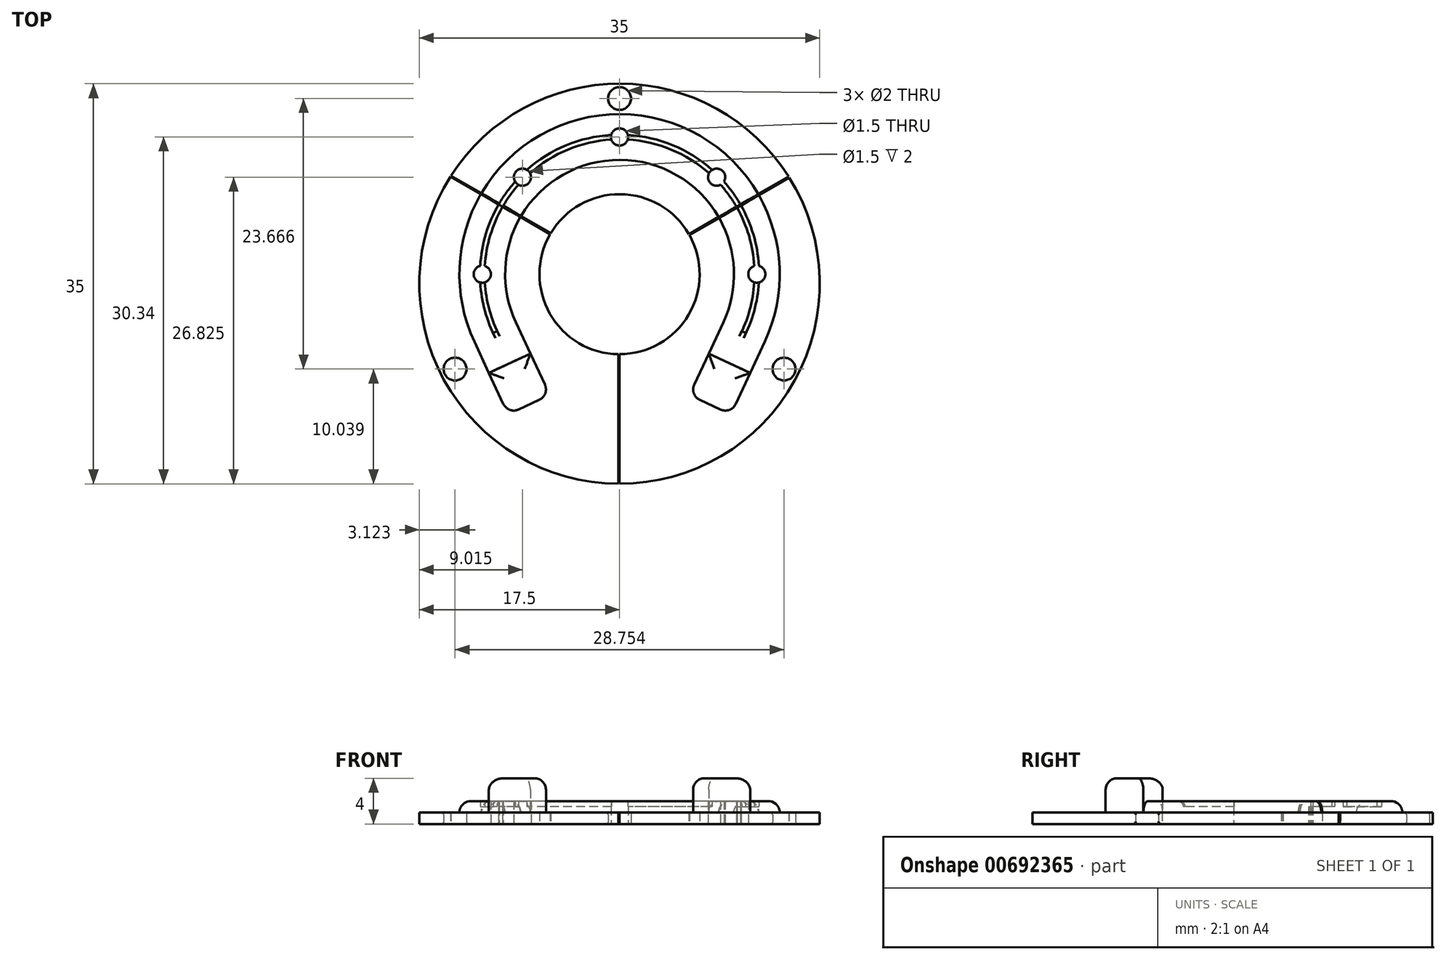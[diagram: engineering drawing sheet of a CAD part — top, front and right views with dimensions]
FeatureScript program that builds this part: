
annotation { "Feature Type Name" : "Feature", "Feature Type Description" : "" }
export const myFeature = defineFeature(function(context is Context, id is Id, definition is map)
    precondition{}
    {
        {
            var Q0;
            Q0=qCreatedBy(makeId("Top.planeOp"),FACE);
            var sketch = newSketch(context, id + "F0", { "sketchPlane" : qUnion([Q0])});
            skFitSpline(sketch, "E0", {"points": [v(-1.42, -15.36) * mm, v(0, -15.45) * mm, v(1.43, -15.36) * mm, v(3.29, -15.03) * mm, v(5.07, -14.39) * mm, v(6.72, -13.46) * mm, v(8.27, -12.35) * mm, v(9.96, -10.69) * mm, v(11.3, -8.73) * mm, v(12.17, -7) * mm, v(12.88, -5.22) * mm, v(13.35, -3.36) * mm, v(13.59, -1.45) * mm, v(13.65, 0) * mm, v(13.59, 1.45) * mm, v(13.35, 3.36) * mm, v(12.88, 5.23) * mm, v(12.17, 7) * mm, v(11.3, 8.73) * mm, v(9.96, 10.69) * mm, v(8.27, 12.35) * mm, v(6.72, 13.46) * mm, v(5.07, 14.4) * mm, v(3.29, 15.04) * mm, v(1.43, 15.37) * mm, v(0, 15.45) * mm, v(-1.42, 15.37) * mm, v(-3.28, 15.04) * mm, v(-5.07, 14.4) * mm, v(-6.72, 13.46) * mm, v(-8.26, 12.35) * mm, v(-9.96, 10.69) * mm, v(-11.3, 8.73) * mm, v(-12.17, 7) * mm, v(-12.87, 5.23) * mm, v(-13.35, 3.36) * mm, v(-13.58, 1.45) * mm, v(-13.64, 0) * mm, v(-13.58, -1.45) * mm, v(-13.35, -3.36) * mm, v(-12.87, -5.22) * mm, v(-12.17, -7) * mm, v(-11.3, -8.73) * mm, v(-9.96, -10.69) * mm, v(-8.26, -12.35) * mm, v(-6.72, -13.46) * mm, v(-5.07, -14.39) * mm, v(-3.28, -15.03) * mm, v(-1.42, -15.36) * mm, v(0, -15.45) * mm, v(1.43, -15.36) * mm]});
            skLineSegment(sketch, "E1", {"start": v(0, 0) * mm, "end": v(-9.06, -4.23) * mm});
            skLineSegment(sketch, "E2", {"start": v(0, 0) * mm, "end": v(9.06, -4.23) * mm});
            skLineSegment(sketch, "E3", {"start": v(-9.06, -4.23) * mm, "end": v(-9.06, -4.23) * mm});
            skLineSegment(sketch, "E4", {"start": v(9.06, -4.23) * mm, "end": v(12.69, -5.92) * mm});
            skLineSegment(sketch, "E5", {"start": v(-9.06, -4.23) * mm, "end": v(-12.69, -5.92) * mm});
            skArc(sketch, "E6", {"start": v(9.06, -4.23) * mm, "mid": v(0, 10) * mm, "end": v(-9.06, -4.23) * mm});
            skArc(sketch, "E7", {"start": v(12.69, -5.92) * mm, "mid": v(0, 14) * mm, "end": v(-12.69, -5.92) * mm});
            skLineSegment(sketch, "E8", {"start": v(-9.06, -4.23) * mm, "end": v(-6.1, -10.57) * mm});
            skLineSegment(sketch, "E9", {"start": v(-6.1, -10.57) * mm, "end": v(-9.73, -12.26) * mm});
            skLineSegment(sketch, "E10", {"start": v(-9.73, -12.26) * mm, "end": v(-12.69, -5.92) * mm});
            skLineSegment(sketch, "E11", {"start": v(9.06, -4.23) * mm, "end": v(6.1, -10.57) * mm});
            skLineSegment(sketch, "E12", {"start": v(6.1, -10.57) * mm, "end": v(9.73, -12.26) * mm});
            skLineSegment(sketch, "E13", {"start": v(9.73, -12.26) * mm, "end": v(12.69, -5.92) * mm});
            skLineSegment(sketch, "E14", {"start": v(-7.8, -6.95) * mm, "end": v(-11.42, -8.64) * mm});
            skLineSegment(sketch, "E15", {"start": v(7.8, -6.95) * mm, "end": v(11.42, -8.64) * mm});
            skArc(sketch, "E16", {"start": v(-10.88, -5.07) * mm, "mid": v(0, 12) * mm, "end": v(10.88, -5.07) * mm});
            skLineSegment(sketch, "E17", {"start": v(0, 0) * mm, "end": v(8.49, 8.49) * mm});
            skLineSegment(sketch, "E18", {"start": v(0, 0) * mm, "end": v(-8.49, 8.49) * mm});
            skCircle(sketch, "E19", {"center": v(-12, 0) * mm, "radius": 0.75 * mm});
            skCircle(sketch, "E20", {"center": v(12, 0) * mm, "radius": 0.75 * mm});
            skCircle(sketch, "E21", {"center": v(8.49, 8.49) * mm, "radius": 0.75 * mm});
            skCircle(sketch, "E22", {"center": v(-8.49, 8.49) * mm, "radius": 0.75 * mm});
            skCircle(sketch, "E23", {"center": v(0, 12) * mm, "radius": 0.75 * mm});
            skArc(sketch, "E24.0", {"start": v(-10.7, -4.99) * mm, "mid": v(0, 11.8) * mm, "end": v(10.7, -4.99) * mm});
            skArc(sketch, "E25.0", {"start": v(-11.06, -5.16) * mm, "mid": v(0, 12.2) * mm, "end": v(11.06, -5.16) * mm});
            skPoint(sketch, "E26", {"position": v(0, -12.26) * mm});
            skPoint(sketch, "E27", {"position": v(0, -0.84) * mm});
            skCircle(sketch, "E28", {"center": v(0, -0.84) * mm, "radius": 17.5 * mm});
            skCircle(sketch, "E29", {"center": v(0, 0) * mm, "radius": 7 * mm});
            skPoint(sketch, "E30", {"position": v(0, 15.37) * mm});
            skLineSegment(sketch, "E31", {"start": v(0, 0) * mm, "end": v(-19.6, -11.31) * mm});
            skLineSegment(sketch, "E32", {"start": v(0, 0) * mm, "end": v(18.13, -10.47) * mm});
            skPoint(sketch, "E33", {"position": v(-14.38, -8.3) * mm});
            skPoint(sketch, "E34", {"position": v(14.38, -8.3) * mm});
            skCircle(sketch, "E35", {"center": v(0, 15.37) * mm, "radius": 1 * mm});
            skCircle(sketch, "E36", {"center": v(14.38, -8.3) * mm, "radius": 1 * mm});
            skCircle(sketch, "E37", {"center": v(-14.38, -8.3) * mm, "radius": 1 * mm});
            skLineSegment(sketch, "E38", {"start": v(0, 0) * mm, "end": v(0, -24.87) * mm});
            skLineSegment(sketch, "E39", {"start": v(0, 0) * mm, "end": v(19.52, 11.27) * mm});
            skLineSegment(sketch, "E40", {"start": v(0, 0) * mm, "end": v(-24.6, 14.2) * mm});
            skLineSegment(sketch, "E41.0", {"start": v(0.05, 0.09) * mm, "end": v(-24.54, 14.28) * mm});
            skLineSegment(sketch, "E42.0", {"start": v(0.05, -0.09) * mm, "end": v(19.57, 11.18) * mm});
            skLineSegment(sketch, "E43.0", {"start": v(-0.1, 0) * mm, "end": v(-0.1, -24.87) * mm});
            skSolve(sketch);
        }
        {
            var Q0;
            {var subQ5=sQuery(id+"F0.wireOp",EDGE,"E18");var subQ6=sQuery(id+"F0.wireOp",EDGE,"E6");var subQ7=makeQuery(id+"F0.imprint","INTERSECT",VERTEX,{"derivedFrom":[subQ6,subQ5]});Q0=makeQuery(id+"F0.imprint","IMPRINT",FACE,{"disambiguationData":[TD([[makeQuery(id+"F0.imprint","IMPRINT",EDGE,{"disambiguationData":[TD([[subQ7,-1.0]])],"derivedFrom":subQ6}),-1.0]])]});}
            var Q1;
            {var subQ0=sQuery(id+"F0.wireOp",EDGE,"E14");Q1=makeQuery(id+"F0.imprint","IMPRINT",FACE,{"disambiguationData":[TD([[makeQuery(id+"F0.imprint","IMPRINT",EDGE,{"derivedFrom":subQ0}),-1.0]])]});}
            var Q2;
            {var subQ0=sQuery(id+"F0.wireOp",EDGE,"E15");Q2=makeQuery(id+"F0.imprint","IMPRINT",FACE,{"disambiguationData":[TD([[makeQuery(id+"F0.imprint","IMPRINT",EDGE,{"derivedFrom":subQ0}),1.0]])]});}
            var Q3;
            {var subQ3=sQuery(id+"F0.wireOp",EDGE,"E39");var subQ7=sQuery(id+"F0.wireOp",EDGE,"E6");var subQ9=makeQuery(id+"F0.imprint","INTERSECT",VERTEX,{"derivedFrom":[subQ7,subQ3]});Q3=makeQuery(id+"F0.imprint","IMPRINT",FACE,{"disambiguationData":[TD([[makeQuery(id+"F0.imprint","IMPRINT",EDGE,{"disambiguationData":[TD([[subQ9,-1.0]])],"derivedFrom":subQ7}),-1.0]])]});}
            var Q4;
            {var subQ1=sQuery(id+"F0.wireOp",EDGE,"E17");var subQ9=sQuery(id+"F0.wireOp",EDGE,"E6");var subQ10=makeQuery(id+"F0.imprint","INTERSECT",VERTEX,{"derivedFrom":[subQ9,subQ1]});Q4=makeQuery(id+"F0.imprint","IMPRINT",FACE,{"disambiguationData":[TD([[makeQuery(id+"F0.imprint","IMPRINT",EDGE,{"disambiguationData":[TD([[subQ10,-1.0]])],"derivedFrom":subQ9}),-1.0]])]});}
            var Q5;
            {var subQ1=sQuery(id+"F0.wireOp",EDGE,"E5");var subQ4=makeQuery(id+"F0.imprint","INTERSECT",VERTEX,{"derivedFrom":[subQ1,sQuery(id+"F0.wireOp",EDGE,"E16")]});Q5=makeQuery(id+"F0.imprint","IMPRINT",FACE,{"disambiguationData":[TD([[makeQuery(id+"F0.imprint","IMPRINT",EDGE,{"disambiguationData":[TD([[subQ4,1.0]])],"derivedFrom":subQ1}),1.0]])]});}
            var Q6;
            {var subQ1=sQuery(id+"F0.wireOp",EDGE,"E4");var subQ4=makeQuery(id+"F0.imprint","INTERSECT",VERTEX,{"derivedFrom":[subQ1,sQuery(id+"F0.wireOp",EDGE,"E16")]});Q6=makeQuery(id+"F0.imprint","IMPRINT",FACE,{"disambiguationData":[TD([[makeQuery(id+"F0.imprint","IMPRINT",EDGE,{"disambiguationData":[TD([[subQ4,1.0]])],"derivedFrom":subQ1}),-1.0]])]});}
            var Q7;
            {var subQ6=sQuery(id+"F0.wireOp",EDGE,"E39");var subQ12=sQuery(id+"F0.wireOp",EDGE,"E7");var subQ13=makeQuery(id+"F0.imprint","INTERSECT",VERTEX,{"derivedFrom":[subQ12,subQ6]});Q7=makeQuery(id+"F0.imprint","IMPRINT",FACE,{"disambiguationData":[TD([[makeQuery(id+"F0.imprint","IMPRINT",EDGE,{"disambiguationData":[TD([[subQ13,-1.0]])],"derivedFrom":subQ12}),1.0]])]});}
            var Q8;
            {var subQ0=sQuery(id+"F0.wireOp",EDGE,"E24.0");var subQ1=sQuery(id+"F0.wireOp",EDGE,"E20");var subQ2=makeQuery(id+"F0.imprint","INTERSECT",VERTEX,{"disambiguationData":[OD(0.0)],"derivedFrom":[subQ1,subQ0]});Q8=makeQuery(id+"F0.imprint","IMPRINT",FACE,{"disambiguationData":[TD([[makeQuery(id+"F0.imprint","IMPRINT",EDGE,{"disambiguationData":[TD([[subQ2,-1.0]])],"derivedFrom":subQ1}),-1.0]])]});}
            var Q9;
            {var subQ0=sQuery(id+"F0.wireOp",EDGE,"E24.0");var subQ3=sQuery(id+"F0.wireOp",EDGE,"E19");var subQ5=makeQuery(id+"F0.imprint","INTERSECT",VERTEX,{"disambiguationData":[OD(0.0)],"derivedFrom":[subQ3,subQ0]});Q9=makeQuery(id+"F0.imprint","IMPRINT",FACE,{"disambiguationData":[TD([[makeQuery(id+"F0.imprint","IMPRINT",EDGE,{"disambiguationData":[TD([[subQ5,1.0]])],"derivedFrom":subQ3}),-1.0]])]});}
            var Q10;
            {var subQ0=sQuery(id+"F0.wireOp",EDGE,"E25.0");var subQ3=sQuery(id+"F0.wireOp",EDGE,"E19");var subQ5=makeQuery(id+"F0.imprint","INTERSECT",VERTEX,{"disambiguationData":[OD(0.0)],"derivedFrom":[subQ3,subQ0]});Q10=makeQuery(id+"F0.imprint","IMPRINT",FACE,{"disambiguationData":[TD([[makeQuery(id+"F0.imprint","IMPRINT",EDGE,{"disambiguationData":[TD([[subQ5,-1.0]])],"derivedFrom":subQ3}),-1.0]])]});}
            var Q11;
            {var subQ0=sQuery(id+"F0.wireOp",EDGE,"E25.0");var subQ1=sQuery(id+"F0.wireOp",EDGE,"E20");var subQ2=makeQuery(id+"F0.imprint","INTERSECT",VERTEX,{"disambiguationData":[OD(0.0)],"derivedFrom":[subQ1,subQ0]});Q11=makeQuery(id+"F0.imprint","IMPRINT",FACE,{"disambiguationData":[TD([[makeQuery(id+"F0.imprint","IMPRINT",EDGE,{"disambiguationData":[TD([[subQ2,1.0]])],"derivedFrom":subQ1}),-1.0]])]});}
            extrude(context, id + "F1", {"entities" : qUnion([Q0, Q1, Q2, Q3, Q4, Q5, Q6, Q7, Q8, Q9, Q10, Q11]), "depth" : 2 * mm, "offsetDistance" : 25 * mm});
        }
        {
            var Q0;
            {var subQ3=sQuery(id+"F0.wireOp",EDGE,"E14");Q0=makeQuery(id+"F0.imprint","IMPRINT",FACE,{"disambiguationData":[TD([[makeQuery(id+"F0.imprint","IMPRINT",EDGE,{"derivedFrom":subQ3}),1.0]])]});}
            var Q1;
            {var subQ0=sQuery(id+"F0.wireOp",EDGE,"E12");Q1=makeQuery(id+"F0.imprint","IMPRINT",FACE,{"disambiguationData":[TD([[makeQuery(id+"F0.imprint","IMPRINT",EDGE,{"derivedFrom":subQ0}),1.0]])]});}
            extrude(context, id + "F2", {"entities" : qUnion([Q0, Q1]), "operationType" : NewBodyOperationType.ADD, "depth" : 4 * mm, "offsetDistance" : 25 * mm});
        }
        {
            var Q0;
            Q0=makeQuery(id+"F0.imprint","IMPRINT",FACE,{"disambiguationData":[TD([[makeQuery(id+"F0.imprint","IMPRINT",EDGE,{"derivedFrom":sQuery(id+"F0.wireOp",EDGE,"SsNEdbVM-fstB-OzVH-ysRz-rdV2LMAxBO9n")}),-1.0]])]});
            var Q1;
            {var subQ0=sQuery(id+"F0.wireOp",EDGE,"E16");var subQ1=sQuery(id+"F0.wireOp",EDGE,"E5");var subQ2=makeQuery(id+"F0.imprint","INTERSECT",VERTEX,{"derivedFrom":[subQ1,subQ0]});Q1=makeQuery(id+"F0.imprint","IMPRINT",FACE,{"disambiguationData":[TD([[makeQuery(id+"F0.imprint","IMPRINT",EDGE,{"disambiguationData":[TD([[subQ2,-1.0]])],"derivedFrom":subQ1}),-1.0]])]});}
            var Q2;
            {var subQ0=sQuery(id+"F0.wireOp",EDGE,"E16");var subQ1=sQuery(id+"F0.wireOp",EDGE,"E5");var subQ2=makeQuery(id+"F0.imprint","INTERSECT",VERTEX,{"derivedFrom":[subQ1,subQ0]});Q2=makeQuery(id+"F0.imprint","IMPRINT",FACE,{"disambiguationData":[TD([[makeQuery(id+"F0.imprint","IMPRINT",EDGE,{"disambiguationData":[TD([[subQ2,1.0]])],"derivedFrom":subQ1}),-1.0]])]});}
            var Q3;
            {var subQ0=sQuery(id+"F0.wireOp",EDGE,"E19");var subQ1=sQuery(id+"F0.wireOp",EDGE,"E16");var subQ2=makeQuery(id+"F0.imprint","INTERSECT",VERTEX,{"disambiguationData":[OD(1.0)],"derivedFrom":[subQ1,subQ0]});Q3=makeQuery(id+"F0.imprint","IMPRINT",FACE,{"disambiguationData":[TD([[makeQuery(id+"F0.imprint","IMPRINT",EDGE,{"disambiguationData":[TD([[subQ2,-1.0]])],"derivedFrom":subQ1}),1.0]])]});}
            var Q4;
            {var subQ0=sQuery(id+"F0.wireOp",EDGE,"E19");var subQ1=sQuery(id+"F0.wireOp",EDGE,"E16");var subQ2=makeQuery(id+"F0.imprint","INTERSECT",VERTEX,{"disambiguationData":[OD(1.0)],"derivedFrom":[subQ1,subQ0]});Q4=makeQuery(id+"F0.imprint","IMPRINT",FACE,{"disambiguationData":[TD([[makeQuery(id+"F0.imprint","IMPRINT",EDGE,{"disambiguationData":[TD([[subQ2,-1.0]])],"derivedFrom":subQ1}),-1.0]])]});}
            var Q5;
            {var subQ0=sQuery(id+"F0.wireOp",EDGE,"E16");var subQ1=sQuery(id+"F0.wireOp",EDGE,"E4");var subQ2=makeQuery(id+"F0.imprint","INTERSECT",VERTEX,{"derivedFrom":[subQ1,subQ0]});Q5=makeQuery(id+"F0.imprint","IMPRINT",FACE,{"disambiguationData":[TD([[makeQuery(id+"F0.imprint","IMPRINT",EDGE,{"disambiguationData":[TD([[subQ2,1.0]])],"derivedFrom":subQ1}),1.0]])]});}
            var Q6;
            {var subQ0=sQuery(id+"F0.wireOp",EDGE,"E16");var subQ1=sQuery(id+"F0.wireOp",EDGE,"E4");var subQ2=makeQuery(id+"F0.imprint","INTERSECT",VERTEX,{"derivedFrom":[subQ1,subQ0]});Q6=makeQuery(id+"F0.imprint","IMPRINT",FACE,{"disambiguationData":[TD([[makeQuery(id+"F0.imprint","IMPRINT",EDGE,{"disambiguationData":[TD([[subQ2,-1.0]])],"derivedFrom":subQ1}),1.0]])]});}
            var Q7;
            {var subQ0=sQuery(id+"F0.wireOp",EDGE,"E21");var subQ1=sQuery(id+"F0.wireOp",EDGE,"E16");var subQ2=makeQuery(id+"F0.imprint","INTERSECT",VERTEX,{"disambiguationData":[OD(1.0)],"derivedFrom":[subQ1,subQ0]});Q7=makeQuery(id+"F0.imprint","IMPRINT",FACE,{"disambiguationData":[TD([[makeQuery(id+"F0.imprint","IMPRINT",EDGE,{"disambiguationData":[TD([[subQ2,-1.0]])],"derivedFrom":subQ1}),1.0]])]});}
            var Q8;
            {var subQ0=sQuery(id+"F0.wireOp",EDGE,"E21");var subQ1=sQuery(id+"F0.wireOp",EDGE,"E16");var subQ2=makeQuery(id+"F0.imprint","INTERSECT",VERTEX,{"disambiguationData":[OD(1.0)],"derivedFrom":[subQ1,subQ0]});Q8=makeQuery(id+"F0.imprint","IMPRINT",FACE,{"disambiguationData":[TD([[makeQuery(id+"F0.imprint","IMPRINT",EDGE,{"disambiguationData":[TD([[subQ2,-1.0]])],"derivedFrom":subQ1}),-1.0]])]});}
            var Q9;
            {var subQ0=sQuery(id+"F0.wireOp",EDGE,"E23");var subQ1=sQuery(id+"F0.wireOp",EDGE,"E16");var subQ2=makeQuery(id+"F0.imprint","INTERSECT",VERTEX,{"disambiguationData":[OD(1.0)],"derivedFrom":[subQ1,subQ0]});Q9=makeQuery(id+"F0.imprint","IMPRINT",FACE,{"disambiguationData":[TD([[makeQuery(id+"F0.imprint","IMPRINT",EDGE,{"disambiguationData":[TD([[subQ2,-1.0]])],"derivedFrom":subQ1}),-1.0]])]});}
            var Q10;
            {var subQ0=sQuery(id+"F0.wireOp",EDGE,"E23");var subQ1=sQuery(id+"F0.wireOp",EDGE,"E16");var subQ2=makeQuery(id+"F0.imprint","INTERSECT",VERTEX,{"disambiguationData":[OD(1.0)],"derivedFrom":[subQ1,subQ0]});Q10=makeQuery(id+"F0.imprint","IMPRINT",FACE,{"disambiguationData":[TD([[makeQuery(id+"F0.imprint","IMPRINT",EDGE,{"disambiguationData":[TD([[subQ2,-1.0]])],"derivedFrom":subQ1}),1.0]])]});}
            var Q11;
            {var subQ0=sQuery(id+"F0.wireOp",EDGE,"E22");var subQ1=sQuery(id+"F0.wireOp",EDGE,"E16");var subQ2=makeQuery(id+"F0.imprint","INTERSECT",VERTEX,{"disambiguationData":[OD(1.0)],"derivedFrom":[subQ1,subQ0]});Q11=makeQuery(id+"F0.imprint","IMPRINT",FACE,{"disambiguationData":[TD([[makeQuery(id+"F0.imprint","IMPRINT",EDGE,{"disambiguationData":[TD([[subQ2,-1.0]])],"derivedFrom":subQ1}),-1.0]])]});}
            var Q12;
            {var subQ0=sQuery(id+"F0.wireOp",EDGE,"E22");var subQ1=sQuery(id+"F0.wireOp",EDGE,"E16");var subQ2=makeQuery(id+"F0.imprint","INTERSECT",VERTEX,{"disambiguationData":[OD(1.0)],"derivedFrom":[subQ1,subQ0]});Q12=makeQuery(id+"F0.imprint","IMPRINT",FACE,{"disambiguationData":[TD([[makeQuery(id+"F0.imprint","IMPRINT",EDGE,{"disambiguationData":[TD([[subQ2,-1.0]])],"derivedFrom":subQ1}),1.0]])]});}
            var Q13;
            {var subQ0=sQuery(id+"F0.wireOp",EDGE,"E41.0");var subQ1=sQuery(id+"F0.wireOp",EDGE,"E16");var subQ2=makeQuery(id+"F0.imprint","INTERSECT",VERTEX,{"derivedFrom":[subQ1,subQ0]});Q13=makeQuery(id+"F0.imprint","IMPRINT",FACE,{"disambiguationData":[TD([[makeQuery(id+"F0.imprint","IMPRINT",EDGE,{"disambiguationData":[TD([[subQ2,-1.0]])],"derivedFrom":subQ1}),1.0]])]});}
            var Q14;
            {var subQ0=sQuery(id+"F0.wireOp",EDGE,"E41.0");var subQ1=sQuery(id+"F0.wireOp",EDGE,"E16");var subQ2=makeQuery(id+"F0.imprint","INTERSECT",VERTEX,{"derivedFrom":[subQ1,subQ0]});Q14=makeQuery(id+"F0.imprint","IMPRINT",FACE,{"disambiguationData":[TD([[makeQuery(id+"F0.imprint","IMPRINT",EDGE,{"disambiguationData":[TD([[subQ2,-1.0]])],"derivedFrom":subQ1}),-1.0]])]});}
            var Q15;
            {var subQ0=sQuery(id+"F0.wireOp",EDGE,"E42.0");var subQ1=sQuery(id+"F0.wireOp",EDGE,"E16");var subQ2=makeQuery(id+"F0.imprint","INTERSECT",VERTEX,{"derivedFrom":[subQ1,subQ0]});Q15=makeQuery(id+"F0.imprint","IMPRINT",FACE,{"disambiguationData":[TD([[makeQuery(id+"F0.imprint","IMPRINT",EDGE,{"disambiguationData":[TD([[subQ2,-1.0]])],"derivedFrom":subQ1}),1.0]])]});}
            var Q16;
            {var subQ0=sQuery(id+"F0.wireOp",EDGE,"E42.0");var subQ1=sQuery(id+"F0.wireOp",EDGE,"E16");var subQ2=makeQuery(id+"F0.imprint","INTERSECT",VERTEX,{"derivedFrom":[subQ1,subQ0]});Q16=makeQuery(id+"F0.imprint","IMPRINT",FACE,{"disambiguationData":[TD([[makeQuery(id+"F0.imprint","IMPRINT",EDGE,{"disambiguationData":[TD([[subQ2,-1.0]])],"derivedFrom":subQ1}),-1.0]])]});}
            extrude(context, id + "F3", {"entities" : qUnion([Q0, Q1, Q2, Q3, Q4, Q5, Q6, Q7, Q8, Q9, Q10, Q11, Q12, Q13, Q14, Q15, Q16]), "operationType" : NewBodyOperationType.ADD, "depth" : 1.5 * mm, "offsetDistance" : 25 * mm});
        }
        {
            var Q0;
            Q0=makeQuery(id+"F1.opExtrude","CAP_EDGE",EDGE,{"disambiguationData":[OSD([sQuery(id+"F0.wireOp",EDGE,"E7")])],"isStart":false});
            var Q1;
            Q1=makeQuery(id+"F1.opExtrude","CAP_EDGE",EDGE,{"disambiguationData":[OSD([sQuery(id+"F0.wireOp",EDGE,"E6")])],"isStart":false});
            var Q2;
            Q2=makeQuery(id+"F2.opExtrude","CAP_EDGE",EDGE,{"disambiguationData":[OSD([sQuery(id+"F0.wireOp",EDGE,"E12")])],"isStart":false});
            var Q3;
            Q3=makeQuery(id+"F2.opExtrude","SWEPT_EDGE",EDGE,{"disambiguationData":[OSD([sQuery(id+"F0.wireOp",EDGE,"E12"),sQuery(id+"F0.wireOp",EDGE,"E13")])]});
            var Q4;
            Q4=makeQuery(id+"F2.opExtrude","CAP_EDGE",EDGE,{"disambiguationData":[OSD([sQuery(id+"F0.wireOp",EDGE,"E13")])],"isStart":false});
            var Q5;
            Q5=makeQuery(id+"F2.opExtrude","CAP_EDGE",EDGE,{"disambiguationData":[OSD([sQuery(id+"F0.wireOp",EDGE,"E11")])],"isStart":false});
            var Q6;
            Q6=makeQuery(id+"F2.opExtrude","CAP_EDGE",EDGE,{"disambiguationData":[OSD([sQuery(id+"F0.wireOp",EDGE,"E8")])],"isStart":false});
            var Q7;
            Q7=makeQuery(id+"F2.opExtrude","CAP_EDGE",EDGE,{"disambiguationData":[OSD([sQuery(id+"F0.wireOp",EDGE,"E9")])],"isStart":false});
            var Q8;
            Q8=makeQuery(id+"F2.opExtrude","CAP_EDGE",EDGE,{"disambiguationData":[OSD([sQuery(id+"F0.wireOp",EDGE,"E10")])],"isStart":false});
            var Q9;
            Q9=makeQuery(id+"F2.opExtrude","CAP_EDGE",EDGE,{"disambiguationData":[OSD([sQuery(id+"F0.wireOp",EDGE,"E14")])],"isStart":false});
            var Q10;
            Q10=makeQuery(id+"F2.opExtrude","CAP_EDGE",EDGE,{"disambiguationData":[OSD([sQuery(id+"F0.wireOp",EDGE,"E15")])],"isStart":false});
            var Q11;
            Q11=makeQuery(id+"F2.opExtrude","SWEPT_EDGE",EDGE,{"disambiguationData":[OSD([sQuery(id+"F0.wireOp",EDGE,"E11"),sQuery(id+"F0.wireOp",EDGE,"E12")])]});
            var Q12;
            Q12=makeQuery(id+"F2.opExtrude","SWEPT_EDGE",EDGE,{"disambiguationData":[OSD([sQuery(id+"F0.wireOp",EDGE,"E8"),sQuery(id+"F0.wireOp",EDGE,"E9")])]});
            var Q13;
            Q13=makeQuery(id+"F2.opExtrude","SWEPT_EDGE",EDGE,{"disambiguationData":[OSD([sQuery(id+"F0.wireOp",EDGE,"E9"),sQuery(id+"F0.wireOp",EDGE,"E10")])]});
            fillet(context, id + "F4", {"entities" : qUnion([Q0, Q1, Q2, Q3, Q4, Q5, Q6, Q7, Q8, Q9, Q10, Q11, Q12, Q13]), "radius" : 1 * mm, "tangentPropagation" : true, "allowEdgeOverflow" : false});
        }
        {
            var Q0;
            {var subQ0=sQuery(id+"F0.wireOp",EDGE,"E24.0");Q0=makeQuery(id+"F1.opExtrude","CAP_EDGE",EDGE,{"disambiguationData":[OSD([subQ0]),TDD([makeQuery(id+"F0.imprint","IMPRINT",EDGE,{"disambiguationData":[TD([[makeQuery(id+"F0.imprint","INTERSECT",VERTEX,{"derivedFrom":[sQuery(id+"F0.wireOp",EDGE,"E5"),subQ0]}),-1.0]])],"derivedFrom":subQ0})])],"isStart":false});}
            var Q1;
            {var subQ0=sQuery(id+"F0.wireOp",EDGE,"E25.0");Q1=makeQuery(id+"F1.opExtrude","CAP_EDGE",EDGE,{"disambiguationData":[OSD([subQ0]),TDD([makeQuery(id+"F0.imprint","IMPRINT",EDGE,{"disambiguationData":[TD([[makeQuery(id+"F0.imprint","INTERSECT",VERTEX,{"derivedFrom":[sQuery(id+"F0.wireOp",EDGE,"E5"),subQ0]}),-1.0]])],"derivedFrom":subQ0})])],"isStart":false});}
            var Q2;
            Q2=makeQuery(id+"F1.opExtrude","CAP_EDGE",EDGE,{"disambiguationData":[OSD([sQuery(id+"F0.wireOp",EDGE,"E5")])],"isStart":false});
            var Q3;
            {var subQ0=sQuery(id+"F0.wireOp",EDGE,"E25.0");Q3=makeQuery(id+"F1.opExtrude","CAP_EDGE",EDGE,{"disambiguationData":[OSD([subQ0]),TDD([makeQuery(id+"F0.imprint","IMPRINT",EDGE,{"disambiguationData":[TD([[makeQuery(id+"F0.imprint","INTERSECT",VERTEX,{"disambiguationData":[OD(0.0)],"derivedFrom":[sQuery(id+"F0.wireOp",EDGE,"E19"),subQ0]}),-1.0]])],"derivedFrom":subQ0})])],"isStart":false});}
            var Q4;
            {var subQ0=sQuery(id+"F0.wireOp",EDGE,"E24.0");Q4=makeQuery(id+"F1.opExtrude","CAP_EDGE",EDGE,{"disambiguationData":[OSD([subQ0]),TDD([makeQuery(id+"F0.imprint","IMPRINT",EDGE,{"disambiguationData":[TD([[makeQuery(id+"F0.imprint","INTERSECT",VERTEX,{"disambiguationData":[OD(0.0)],"derivedFrom":[sQuery(id+"F0.wireOp",EDGE,"E19"),subQ0]}),-1.0]])],"derivedFrom":subQ0})])],"isStart":false});}
            var Q5;
            {var subQ0=sQuery(id+"F0.wireOp",EDGE,"E24.0");Q5=makeQuery(id+"F1.opExtrude","CAP_EDGE",EDGE,{"disambiguationData":[OSD([subQ0]),TDD([makeQuery(id+"F0.imprint","IMPRINT",EDGE,{"disambiguationData":[TD([[makeQuery(id+"F0.imprint","INTERSECT",VERTEX,{"derivedFrom":[sQuery(id+"F0.wireOp",EDGE,"E4"),subQ0]}),1.0]])],"derivedFrom":subQ0})])],"isStart":false});}
            var Q6;
            {var subQ0=sQuery(id+"F0.wireOp",EDGE,"E25.0");Q6=makeQuery(id+"F1.opExtrude","CAP_EDGE",EDGE,{"disambiguationData":[OSD([subQ0]),TDD([makeQuery(id+"F0.imprint","IMPRINT",EDGE,{"disambiguationData":[TD([[makeQuery(id+"F0.imprint","INTERSECT",VERTEX,{"derivedFrom":[sQuery(id+"F0.wireOp",EDGE,"E4"),subQ0]}),1.0]])],"derivedFrom":subQ0})])],"isStart":false});}
            var Q7;
            {var subQ0=sQuery(id+"F0.wireOp",EDGE,"E25.0");Q7=makeQuery(id+"F1.opExtrude","CAP_EDGE",EDGE,{"disambiguationData":[OSD([subQ0]),TDD([makeQuery(id+"F0.imprint","IMPRINT",EDGE,{"disambiguationData":[TD([[makeQuery(id+"F0.imprint","INTERSECT",VERTEX,{"disambiguationData":[OD(0.0)],"derivedFrom":[sQuery(id+"F0.wireOp",EDGE,"E22"),subQ0]}),-1.0]])],"derivedFrom":subQ0})])],"isStart":false});}
            var Q8;
            {var subQ0=sQuery(id+"F0.wireOp",EDGE,"E24.0");Q8=makeQuery(id+"F1.opExtrude","CAP_EDGE",EDGE,{"disambiguationData":[OSD([subQ0]),TDD([makeQuery(id+"F0.imprint","IMPRINT",EDGE,{"disambiguationData":[TD([[makeQuery(id+"F0.imprint","INTERSECT",VERTEX,{"disambiguationData":[OD(0.0)],"derivedFrom":[sQuery(id+"F0.wireOp",EDGE,"E22"),subQ0]}),-1.0]])],"derivedFrom":subQ0})])],"isStart":false});}
            var Q9;
            {var subQ0=sQuery(id+"F0.wireOp",EDGE,"E24.0");Q9=makeQuery(id+"F1.opExtrude","CAP_EDGE",EDGE,{"disambiguationData":[OSD([subQ0]),TDD([makeQuery(id+"F0.imprint","IMPRINT",EDGE,{"disambiguationData":[TD([[makeQuery(id+"F0.imprint","INTERSECT",VERTEX,{"disambiguationData":[OD(0.0)],"derivedFrom":[sQuery(id+"F0.wireOp",EDGE,"E21"),subQ0]}),1.0]])],"derivedFrom":subQ0})])],"isStart":false});}
            var Q10;
            {var subQ0=sQuery(id+"F0.wireOp",EDGE,"E25.0");Q10=makeQuery(id+"F1.opExtrude","CAP_EDGE",EDGE,{"disambiguationData":[OSD([subQ0]),TDD([makeQuery(id+"F0.imprint","IMPRINT",EDGE,{"disambiguationData":[TD([[makeQuery(id+"F0.imprint","INTERSECT",VERTEX,{"disambiguationData":[OD(0.0)],"derivedFrom":[sQuery(id+"F0.wireOp",EDGE,"E21"),subQ0]}),1.0]])],"derivedFrom":subQ0})])],"isStart":false});}
            var Q11;
            {var subQ0=sQuery(id+"F0.wireOp",EDGE,"E25.0");Q11=makeQuery(id+"F1.opExtrude","CAP_EDGE",EDGE,{"disambiguationData":[OSD([subQ0]),TDD([makeQuery(id+"F0.imprint","IMPRINT",EDGE,{"disambiguationData":[TD([[makeQuery(id+"F0.imprint","INTERSECT",VERTEX,{"disambiguationData":[OD(0.0)],"derivedFrom":[sQuery(id+"F0.wireOp",EDGE,"E20"),subQ0]}),1.0]])],"derivedFrom":subQ0})])],"isStart":false});}
            var Q12;
            {var subQ0=sQuery(id+"F0.wireOp",EDGE,"E24.0");Q12=makeQuery(id+"F1.opExtrude","CAP_EDGE",EDGE,{"disambiguationData":[OSD([subQ0]),TDD([makeQuery(id+"F0.imprint","IMPRINT",EDGE,{"disambiguationData":[TD([[makeQuery(id+"F0.imprint","INTERSECT",VERTEX,{"disambiguationData":[OD(0.0)],"derivedFrom":[sQuery(id+"F0.wireOp",EDGE,"E20"),subQ0]}),1.0]])],"derivedFrom":subQ0})])],"isStart":false});}
            var Q13;
            Q13=makeQuery(id+"F1.opExtrude","CAP_EDGE",EDGE,{"disambiguationData":[OSD([sQuery(id+"F0.wireOp",EDGE,"E4")])],"isStart":false});
            fillet(context, id + "F5", {"entities" : qUnion([Q0, Q1, Q2, Q3, Q4, Q5, Q6, Q7, Q8, Q9, Q10, Q11, Q12, Q13]), "radius" : 0.5 * mm, "tangentPropagation" : true, "allowEdgeOverflow" : false});
        }
        {
            var Q0;
            {var subQ0=sQuery(id+"F0.wireOp",EDGE,"E17");var subQ1=sQuery(id+"F0.wireOp",EDGE,"E6");var subQ2=makeQuery(id+"F0.imprint","INTERSECT",VERTEX,{"derivedFrom":[subQ1,subQ0]});Q0=makeQuery(id+"F0.imprint","IMPRINT",FACE,{"disambiguationData":[TD([[makeQuery(id+"F0.imprint","IMPRINT",EDGE,{"disambiguationData":[TD([[subQ2,-1.0]])],"derivedFrom":subQ1}),1.0]])]});}
            var Q1;
            {var subQ0=sQuery(id+"F0.wireOp",EDGE,"E9");Q1=makeQuery(id+"F0.imprint","IMPRINT",FACE,{"disambiguationData":[TD([[makeQuery(id+"F0.imprint","IMPRINT",EDGE,{"derivedFrom":subQ0}),-1.0]])]});}
            var Q2;
            {var subQ0=sQuery(id+"F0.wireOp",EDGE,"E12");Q2=makeQuery(id+"F0.imprint","IMPRINT",FACE,{"disambiguationData":[TD([[makeQuery(id+"F0.imprint","IMPRINT",EDGE,{"derivedFrom":subQ0}),1.0]])]});}
            var Q3;
            {var subQ0=sQuery(id+"F0.wireOp",EDGE,"E18");var subQ1=sQuery(id+"F0.wireOp",EDGE,"E6");var subQ2=makeQuery(id+"F0.imprint","INTERSECT",VERTEX,{"derivedFrom":[subQ1,subQ0]});Q3=makeQuery(id+"F0.imprint","IMPRINT",FACE,{"disambiguationData":[TD([[makeQuery(id+"F0.imprint","IMPRINT",EDGE,{"disambiguationData":[TD([[subQ2,-1.0]])],"derivedFrom":subQ1}),1.0]])]});}
            var Q4;
            {var subQ0=sQuery(id+"F0.wireOp",EDGE,"E39");var subQ1=sQuery(id+"F0.wireOp",EDGE,"E6");var subQ2=makeQuery(id+"F0.imprint","INTERSECT",VERTEX,{"derivedFrom":[subQ1,subQ0]});Q4=makeQuery(id+"F0.imprint","IMPRINT",FACE,{"disambiguationData":[TD([[makeQuery(id+"F0.imprint","IMPRINT",EDGE,{"disambiguationData":[TD([[subQ2,-1.0]])],"derivedFrom":subQ1}),1.0]])]});}
            var Q5;
            {var subQ18=sQuery(id+"F0.wireOp",EDGE,"E9");Q5=makeQuery(id+"F0.imprint","IMPRINT",FACE,{"disambiguationData":[TD([[makeQuery(id+"F0.imprint","IMPRINT",EDGE,{"derivedFrom":subQ18}),1.0]])]});}
            var Q6;
            {var subQ1=sQuery(id+"F0.wireOp",EDGE,"E1");var subQ3=sQuery(id+"F0.wireOp",EDGE,"E29");var subQ4=makeQuery(id+"F0.imprint","INTERSECT",VERTEX,{"derivedFrom":[subQ1,subQ3]});Q6=makeQuery(id+"F0.imprint","IMPRINT",FACE,{"disambiguationData":[TD([[makeQuery(id+"F0.imprint","IMPRINT",EDGE,{"disambiguationData":[TD([[subQ4,-1.0]])],"derivedFrom":subQ3}),-1.0]])]});}
            var Q7;
            {var subQ1=sQuery(id+"F0.wireOp",EDGE,"E2");var subQ3=sQuery(id+"F0.wireOp",EDGE,"E29");var subQ4=makeQuery(id+"F0.imprint","INTERSECT",VERTEX,{"derivedFrom":[subQ1,subQ3]});Q7=makeQuery(id+"F0.imprint","IMPRINT",FACE,{"disambiguationData":[TD([[makeQuery(id+"F0.imprint","IMPRINT",EDGE,{"disambiguationData":[TD([[subQ4,1.0]])],"derivedFrom":subQ3}),-1.0]])]});}
            var Q8;
            {var subQ5=sQuery(id+"F0.wireOp",EDGE,"E40");var subQ6=sQuery(id+"F0.wireOp",EDGE,"E28");var subQ7=makeQuery(id+"F0.imprint","INTERSECT",VERTEX,{"derivedFrom":[subQ6,subQ5]});Q8=makeQuery(id+"F0.imprint","IMPRINT",FACE,{"disambiguationData":[TD([[makeQuery(id+"F0.imprint","IMPRINT",EDGE,{"disambiguationData":[TD([[subQ7,-1.0]])],"derivedFrom":subQ6}),1.0]])]});}
            var Q9;
            {var subQ1=sQuery(id+"F0.wireOp",EDGE,"E1");var subQ3=sQuery(id+"F0.wireOp",EDGE,"E29");var subQ4=makeQuery(id+"F0.imprint","INTERSECT",VERTEX,{"derivedFrom":[subQ1,subQ3]});Q9=makeQuery(id+"F0.imprint","IMPRINT",FACE,{"disambiguationData":[TD([[makeQuery(id+"F0.imprint","IMPRINT",EDGE,{"disambiguationData":[TD([[subQ4,1.0]])],"derivedFrom":subQ3}),-1.0]])]});}
            var Q10;
            {var subQ14=sQuery(id+"F0.wireOp",EDGE,"E12");Q10=makeQuery(id+"F0.imprint","IMPRINT",FACE,{"disambiguationData":[TD([[makeQuery(id+"F0.imprint","IMPRINT",EDGE,{"derivedFrom":subQ14}),-1.0]])]});}
            var Q11;
            {var subQ1=sQuery(id+"F0.wireOp",EDGE,"E2");var subQ3=sQuery(id+"F0.wireOp",EDGE,"E29");var subQ4=makeQuery(id+"F0.imprint","INTERSECT",VERTEX,{"derivedFrom":[subQ1,subQ3]});Q11=makeQuery(id+"F0.imprint","IMPRINT",FACE,{"disambiguationData":[TD([[makeQuery(id+"F0.imprint","IMPRINT",EDGE,{"disambiguationData":[TD([[subQ4,-1.0]])],"derivedFrom":subQ3}),-1.0]])]});}
            var Q12;
            Q12=makeQuery(id+"F0.imprint","IMPRINT",FACE,{"disambiguationData":[TD([[makeQuery(id+"F0.imprint","IMPRINT",EDGE,{"derivedFrom":sQuery(id+"F0.wireOp",EDGE,"E35")}),-1.0]])]});
            var Q13;
            {var subQ7=sQuery(id+"F0.wireOp",EDGE,"E42.0");var subQ8=sQuery(id+"F0.wireOp",EDGE,"E28");var subQ9=makeQuery(id+"F0.imprint","INTERSECT",VERTEX,{"derivedFrom":[subQ8,subQ7]});Q13=makeQuery(id+"F0.imprint","IMPRINT",FACE,{"disambiguationData":[TD([[makeQuery(id+"F0.imprint","IMPRINT",EDGE,{"disambiguationData":[TD([[subQ9,1.0]])],"derivedFrom":subQ8}),1.0]])]});}
            extrude(context, id + "F6", {"entities" : qUnion([Q0, Q1, Q2, Q3, Q4, Q5, Q6, Q7, Q8, Q9, Q10, Q11, Q12, Q13]), "operationType" : NewBodyOperationType.ADD, "depth" : 1 * mm, "offsetDistance" : 25 * mm});
        }
        {
            var Q0;
            Q0=makeQuery(id+"F6.opExtrude","CAP_EDGE",EDGE,{"disambiguationData":[OSD([sQuery(id+"F0.wireOp",EDGE,"E36")])],"isStart":true});
            var Q1;
            Q1=makeQuery(id+"F6.opExtrude","CAP_EDGE",EDGE,{"disambiguationData":[OSD([sQuery(id+"F0.wireOp",EDGE,"E36")])],"isStart":false});
            var Q2;
            Q2=makeQuery(id+"F6.opExtrude","CAP_EDGE",EDGE,{"disambiguationData":[OSD([sQuery(id+"F0.wireOp",EDGE,"E35")])],"isStart":false});
            var Q3;
            Q3=makeQuery(id+"F6.opExtrude","CAP_EDGE",EDGE,{"disambiguationData":[OSD([sQuery(id+"F0.wireOp",EDGE,"E35")])],"isStart":true});
            var Q4;
            Q4=makeQuery(id+"F6.opExtrude","CAP_EDGE",EDGE,{"disambiguationData":[OSD([sQuery(id+"F0.wireOp",EDGE,"E37")])],"isStart":false});
            var Q5;
            Q5=makeQuery(id+"F6.opExtrude","CAP_EDGE",EDGE,{"disambiguationData":[OSD([sQuery(id+"F0.wireOp",EDGE,"E37")])],"isStart":true});
            fillet(context, id + "F7", {"entities" : qUnion([Q0, Q1, Q2, Q3, Q4, Q5]), "radius" : 0.2 * mm, "tangentPropagation" : true, "allowEdgeOverflow" : false});
        }
    });
